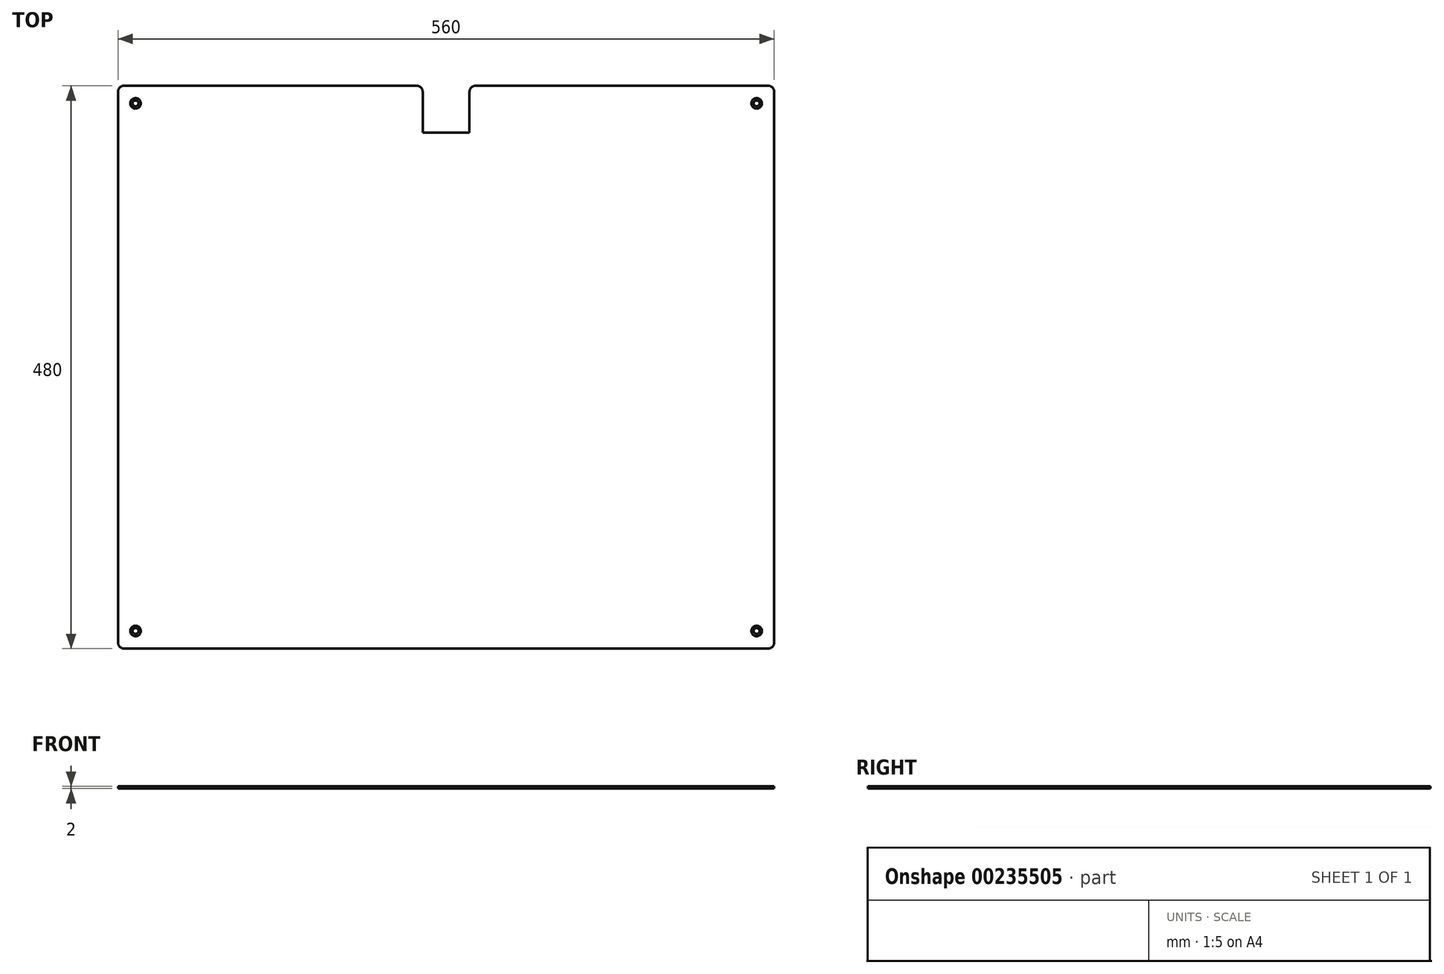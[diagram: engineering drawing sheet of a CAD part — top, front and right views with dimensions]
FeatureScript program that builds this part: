
annotation { "Feature Type Name" : "Feature", "Feature Type Description" : "" }
export const myFeature = defineFeature(function(context is Context, id is Id, definition is map)
    precondition{}
    {
        {
            var Q0;
            Q0=qCreatedBy(makeId("Top.planeOp"),FACE);
            var sketch = newSketch(context, id + "F0", { "sketchPlane" : qUnion([Q0])});
            skLineSegment(sketch, "E0.bottom", {"start": v(275, -240) * mm, "end": v(-275, -240) * mm});
            skLineSegment(sketch, "E0.top", {"start": v(275, 240) * mm, "end": v(25, 240) * mm});
            skLineSegment(sketch, "E0.left", {"start": v(280, -235) * mm, "end": v(280, 235) * mm});
            skLineSegment(sketch, "E0.right", {"start": v(-280, -235) * mm, "end": v(-280, 235) * mm});
            skPoint(sketch, "E0.middle", {"position": v(0, 0) * mm});
            skPoint(sketch, "E1.visualSharp", {"position": v(-280, 240) * mm});
            skArc(sketch, "E1.filletArc", {"start": v(-275, 240) * mm, "mid": v(-278.54, 238.54) * mm, "end": v(-280, 235) * mm});
            skPoint(sketch, "E2.visualSharp", {"position": v(280, -240) * mm});
            skArc(sketch, "E2.filletArc", {"start": v(275, -240) * mm, "mid": v(278.54, -238.54) * mm, "end": v(280, -235) * mm});
            skPoint(sketch, "E3.visualSharp", {"position": v(-280, -240) * mm});
            skArc(sketch, "E3.filletArc", {"start": v(-280, -235) * mm, "mid": v(-278.54, -238.54) * mm, "end": v(-275, -240) * mm});
            skPoint(sketch, "E4.visualSharp", {"position": v(280, 240) * mm});
            skArc(sketch, "E4.filletArc", {"start": v(280, 235) * mm, "mid": v(278.54, 238.54) * mm, "end": v(275, 240) * mm});
            skLineSegment(sketch, "E5.top", {"start": v(-20, 200) * mm, "end": v(20, 200) * mm});
            skLineSegment(sketch, "E5.left", {"start": v(-20, 235) * mm, "end": v(-20, 200) * mm});
            skLineSegment(sketch, "E5.right", {"start": v(20, 235) * mm, "end": v(20, 200) * mm});
            skLineSegment(sketch, "E6.trimOffspring", {"start": v(-25, 240) * mm, "end": v(-275, 240) * mm});
            skPoint(sketch, "E7.visualSharp", {"position": v(-20, 240) * mm});
            skArc(sketch, "E7.filletArc", {"start": v(-20, 235) * mm, "mid": v(-21.46, 238.54) * mm, "end": v(-25, 240) * mm});
            skPoint(sketch, "E8.visualSharp", {"position": v(20, 240) * mm});
            skArc(sketch, "E8.filletArc", {"start": v(25, 240) * mm, "mid": v(21.46, 238.54) * mm, "end": v(20, 235) * mm});
            skSolve(sketch);
        }
        {
            var Q0;
            Q0 = qSketchRegion(id + "F0", true);
            extrude(context, id + "F1", {"entities" : qUnion([Q0]), "depth" : 2 * mm});
        }
        {
            var Q0;
            Q0=makeQuery(id+"F1.opExtrude","CAP_FACE",FACE,{"disambiguationData":[OSD([sQuery(id+"F0.wireOp",EDGE,"E0.bottom"),sQuery(id+"F0.wireOp",EDGE,"E0.top"),sQuery(id+"F0.wireOp",EDGE,"E0.left"),sQuery(id+"F0.wireOp",EDGE,"E0.right"),sQuery(id+"F0.wireOp",EDGE,"E1.filletArc"),sQuery(id+"F0.wireOp",EDGE,"E2.filletArc"),sQuery(id+"F0.wireOp",EDGE,"E3.filletArc"),sQuery(id+"F0.wireOp",EDGE,"E4.filletArc")])],"isStart":false});
            var sketch = newSketch(context, id + "F2", { "sketchPlane" : qUnion([Q0])});
            skCircle(sketch, "E9", {"center": v(265, -225) * mm, "radius": 2 * mm});
            skCircle(sketch, "E10.0.1.0", {"center": v(265, 225) * mm, "radius": 2 * mm});
            skCircle(sketch, "E10.1.0.0", {"center": v(-265, -225) * mm, "radius": 2 * mm});
            skCircle(sketch, "E10.1.1.0", {"center": v(-265, 225) * mm, "radius": 2 * mm});
            skLineSegment(sketch, "E10.direction1", {"start": v(265, -225) * mm, "end": v(-265, -225) * mm, "construction": true});
            skLineSegment(sketch, "E10.direction2", {"start": v(265, -225) * mm, "end": v(265, 225) * mm, "construction": true});
            skSolve(sketch);
        }
        {
            var Q0;
            Q0=sQuery(id+"F2.wireOp",VERTEX,"E10.1.0.0.center");
            var Q1;
            Q1=sQuery(id+"F2.wireOp",VERTEX,"E10.1.1.0.center");
            var Q2;
            Q2=sQuery(id+"F2.wireOp",VERTEX,"E10.0.1.0.center");
            var Q3;
            Q3=sQuery(id+"F2.wireOp",VERTEX,"E9.center");
            var Q4;
            Q4=makeQuery(id+"F1.opExtrude","SWEPT_BODY",BODY,{"disambiguationData":[OSD([sQuery(id+"F0.wireOp",EDGE,"E0.bottom"),sQuery(id+"F0.wireOp",EDGE,"E0.top"),sQuery(id+"F0.wireOp",EDGE,"E0.left"),sQuery(id+"F0.wireOp",EDGE,"E0.right"),sQuery(id+"F0.wireOp",EDGE,"E1.filletArc"),sQuery(id+"F0.wireOp",EDGE,"E2.filletArc"),sQuery(id+"F0.wireOp",EDGE,"E3.filletArc"),sQuery(id+"F0.wireOp",EDGE,"E4.filletArc")])]});
            hole(context, id + "F3", {"style" : HoleStyle.C_SINK, "endStyle" : HoleEndStyle.THROUGH, "standardTappedOrClearance" : lookupTablePath({ "standard" : "ISO", "fit" : "Normal", "size" : "M4", "type" : "Clearance" }), "standardBlindInLast" : lookupTablePath({ "fit" : "Standard", "standard" : "ISO", "size" : "M4", "type" : "Clearance" }), "holeDiameter" : 4.4 * mm, "cSinkDiameter" : 8.96 * mm, "cSinkAngle" : 90 * degree, "locations" : qUnion([Q0, Q1, Q2, Q3]), "scope" : qUnion([Q4]), "isTappedThrough" : true});
        }
    });
